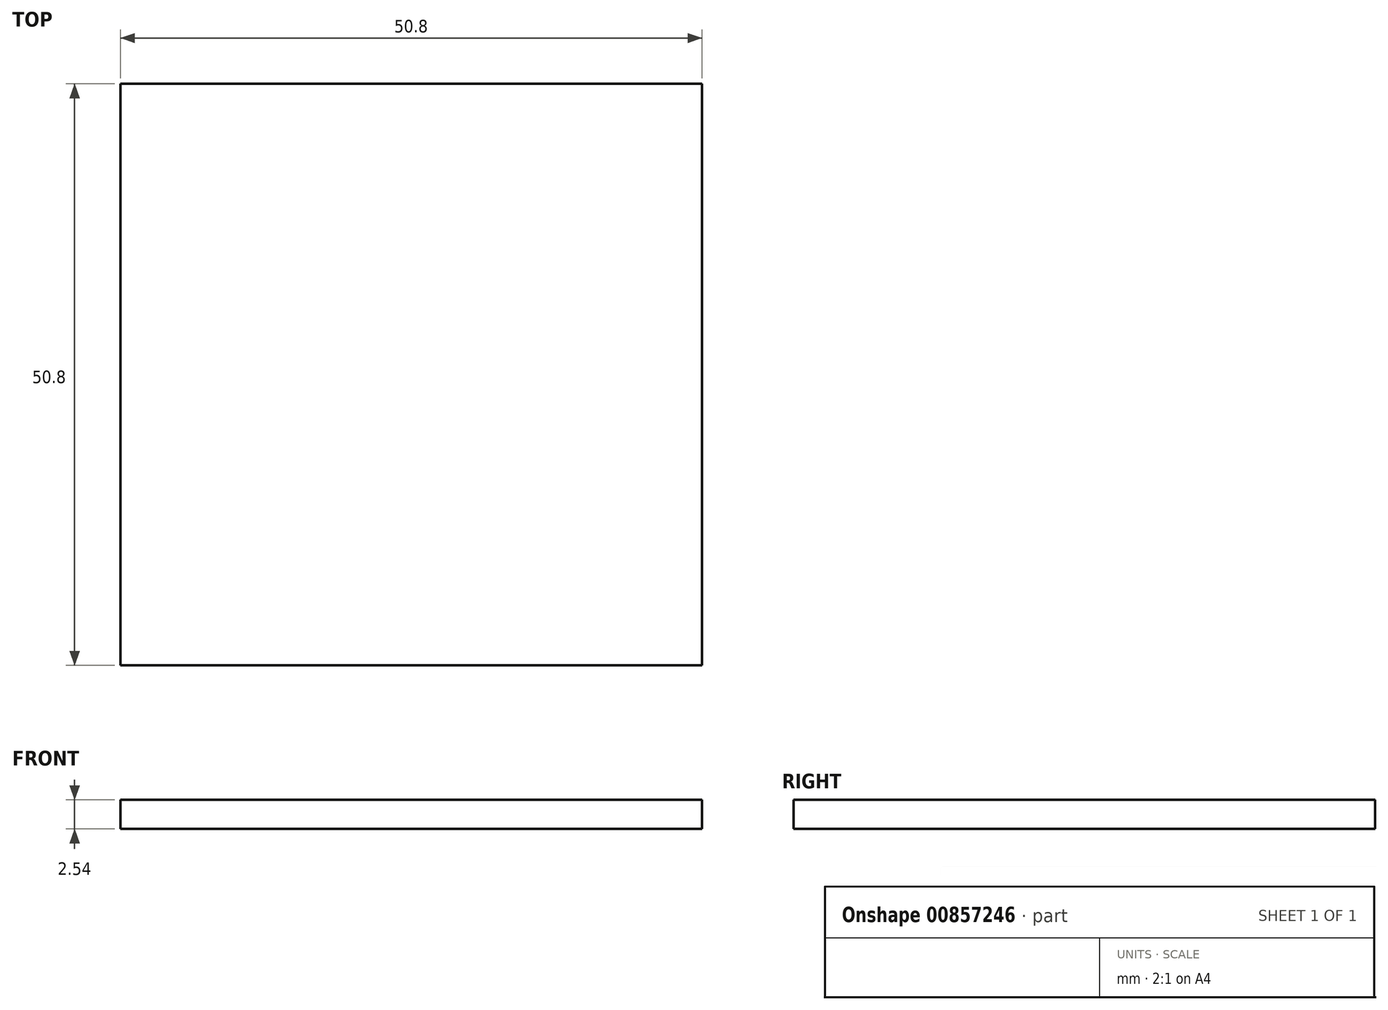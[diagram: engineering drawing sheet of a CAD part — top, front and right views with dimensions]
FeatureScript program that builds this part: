
annotation { "Feature Type Name" : "Feature", "Feature Type Description" : "" }
export const myFeature = defineFeature(function(context is Context, id is Id, definition is map)
    precondition{}
    {
        {
            var Q0;
            Q0=qCreatedBy(makeId("Top.planeOp"),FACE);
            var sketch = newSketch(context, id + "F0", { "sketchPlane" : qUnion([Q0])});
            skLineSegment(sketch, "E0.bottom", {"start": v(-50.8, 72) * mm, "end": v(0, 72) * mm});
            skLineSegment(sketch, "E0.top", {"start": v(-50.8, 21.2) * mm, "end": v(0, 21.2) * mm});
            skLineSegment(sketch, "E0.left", {"start": v(-50.8, 72) * mm, "end": v(-50.8, 21.2) * mm});
            skLineSegment(sketch, "E0.right", {"start": v(0, 72) * mm, "end": v(0, 21.2) * mm});
            skSolve(sketch);
        }
        {
            var Q0;
            Q0=makeQuery(id+"F0.imprint","IMPRINT",FACE,{"disambiguationData":[TD([[makeQuery(id+"F0.imprint","IMPRINT",EDGE,{"derivedFrom":sQuery(id+"F0.wireOp",EDGE,"E0.bottom")}),-1.0]])]});
            extrude(context, id + "F1", {"entities" : qUnion([Q0]), "depth" : 2.54 * mm, "offsetDistance" : 25.4 * mm});
        }
    });
